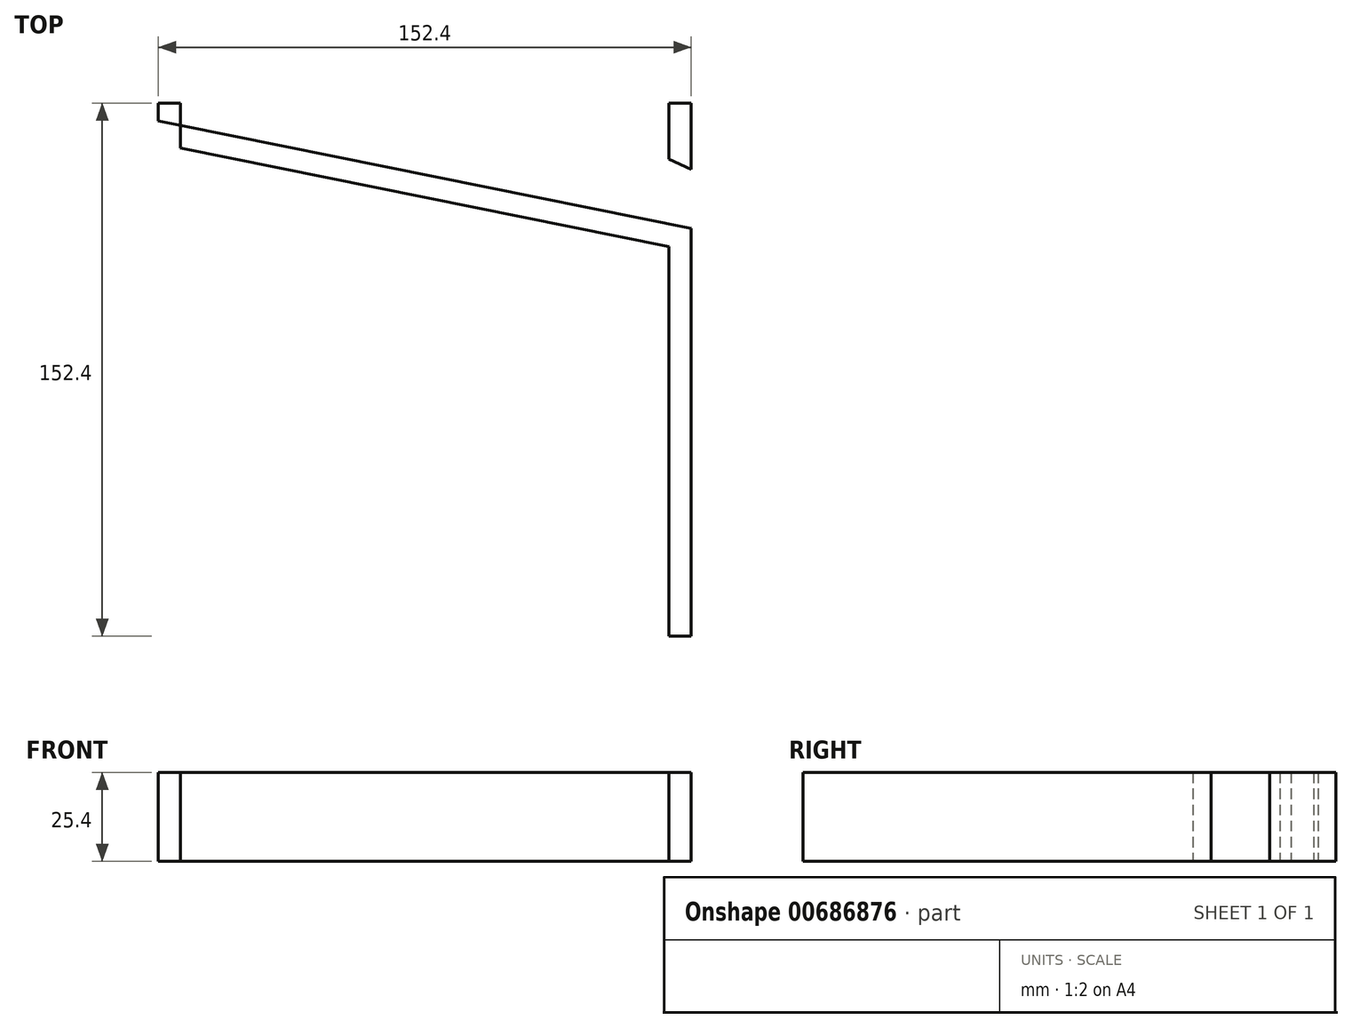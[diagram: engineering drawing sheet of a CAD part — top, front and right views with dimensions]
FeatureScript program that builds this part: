
annotation { "Feature Type Name" : "Feature", "Feature Type Description" : "" }
export const myFeature = defineFeature(function(context is Context, id is Id, definition is map)
    precondition{}
    {
        {
            var Q0;
            Q0=qCreatedBy(makeId("Top.planeOp"),FACE);
            var sketch = newSketch(context, id + "F0", { "sketchPlane" : qUnion([Q0])});
            skLineSegment(sketch, "E0.bottom", {"start": v(-76.85, 75.62) * mm, "end": v(-70.5, 75.62) * mm});
            skLineSegment(sketch, "E0.top", {"start": v(-30.3, -133.93) * mm, "end": v(-23.95, -133.93) * mm});
            skLineSegment(sketch, "E0.left", {"start": v(-76.85, 75.62) * mm, "end": v(-76.85, -76.78) * mm});
            skLineSegment(sketch, "E0.right", {"start": v(-70.5, 75.62) * mm, "end": v(-70.5, -76.78) * mm});
            skLineSegment(sketch, "E1.bottom", {"start": v(69.2, 75.62) * mm, "end": v(75.55, 75.62) * mm});
            skLineSegment(sketch, "E1.left", {"start": v(69.2, 75.62) * mm, "end": v(69.2, -76.78) * mm});
            skLineSegment(sketch, "E1.right", {"start": v(75.55, 75.62) * mm, "end": v(75.55, -76.78) * mm});
            skLineSegment(sketch, "E2.bottom", {"start": v(-70.5, 75.62) * mm, "end": v(69.2, 75.62) * mm});
            skLineSegment(sketch, "E2.top", {"start": v(-70.5, 69.27) * mm, "end": v(69.2, 69.27) * mm});
            skLineSegment(sketch, "E2.left", {"start": v(-70.5, 75.62) * mm, "end": v(-70.5, 69.27) * mm});
            skLineSegment(sketch, "E2.right", {"start": v(69.2, 75.62) * mm, "end": v(69.2, 69.27) * mm});
            skLineSegment(sketch, "E3.bottom", {"start": v(-76.85, 70.55) * mm, "end": v(75.55, 39.85) * mm});
            skLineSegment(sketch, "E3.top", {"start": v(-75.34, 63.76) * mm, "end": v(88.82, 30.7) * mm});
            skLineSegment(sketch, "E3.left", {"start": v(-70.5, 55.09) * mm, "end": v(-70.5, 48.74) * mm});
            skLineSegment(sketch, "E3.right", {"start": v(69.2, 55.09) * mm, "end": v(69.2, 48.74) * mm});
            skLineSegment(sketch, "E4", {"start": v(-76.85, -76.78) * mm, "end": v(-70.5, -76.78) * mm});
            skLineSegment(sketch, "E5", {"start": v(69.2, -76.78) * mm, "end": v(75.55, -76.78) * mm});
            skLineSegment(sketch, "E6", {"start": v(75.55, 22.85) * mm, "end": v(75.55, 16.2) * mm});
            skLineSegment(sketch, "E7.bottom", {"start": v(24, 80.14) * mm, "end": v(176.4, 10.74) * mm});
            skLineSegment(sketch, "E7.top", {"start": v(23.93, 73.2) * mm, "end": v(176.33, 3.8) * mm});
            skSolve(sketch);
        }
        {
            var Q0;
            {var subQ4=sQuery(id+"F0.wireOp",EDGE,"E2.left");Q0=makeQuery(id+"F0.imprint","IMPRINT",FACE,{"disambiguationData":[TD([[makeQuery(id+"F0.imprint","IMPRINT",EDGE,{"derivedFrom":subQ4}),1.0]])]});}
            var Q1;
            {var subQ2=sQuery(id+"F0.wireOp",EDGE,"E3.left");Q1=makeQuery(id+"F0.imprint","IMPRINT",FACE,{"disambiguationData":[TD([[makeQuery(id+"F0.imprint","IMPRINT",EDGE,{"derivedFrom":subQ2}),-1.0]])]});}
            var Q2;
            {var subQ0=sQuery(id+"F0.wireOp",EDGE,"E0.bottom");Q2=makeQuery(id+"F0.imprint","IMPRINT",FACE,{"disambiguationData":[TD([[makeQuery(id+"F0.imprint","IMPRINT",EDGE,{"derivedFrom":subQ0}),-1.0]])]});}
            var Q3;
            {var subQ3=sQuery(id+"F0.wireOp",EDGE,"E3.top");var subQ5=sQuery(id+"F0.wireOp",EDGE,"E1.left");var subQ6=makeQuery(id+"F0.imprint","INTERSECT",VERTEX,{"derivedFrom":[subQ5,subQ3]});Q3=makeQuery(id+"F0.imprint","IMPRINT",FACE,{"disambiguationData":[TD([[makeQuery(id+"F0.imprint","IMPRINT",EDGE,{"disambiguationData":[TD([[subQ6,1.0]])],"derivedFrom":subQ5}),-1.0]])]});}
            var Q4;
            {var subQ0=sQuery(id+"F0.wireOp",EDGE,"E2.right");Q4=makeQuery(id+"F0.imprint","IMPRINT",FACE,{"disambiguationData":[TD([[makeQuery(id+"F0.imprint","IMPRINT",EDGE,{"derivedFrom":subQ0}),-1.0]])]});}
            var Q5;
            {var subQ2=sQuery(id+"F0.wireOp",EDGE,"E1.bottom");Q5=makeQuery(id+"F0.imprint","IMPRINT",FACE,{"disambiguationData":[TD([[makeQuery(id+"F0.imprint","IMPRINT",EDGE,{"derivedFrom":subQ2}),-1.0]])]});}
            var Q6;
            {var subQ0=sQuery(id+"F0.wireOp",EDGE,"E3.right");var subQ1=sQuery(id+"F0.wireOp",EDGE,"E1.left");var subQ2=makeQuery(id+"F0.imprint","INTERSECT",VERTEX,{"disambiguationData":[OD(0.0)],"derivedFrom":[subQ1,subQ0]});Q6=makeQuery(id+"F0.imprint","IMPRINT",FACE,{"disambiguationData":[TD([[makeQuery(id+"F0.imprint","IMPRINT",EDGE,{"disambiguationData":[TD([[subQ2,1.0]])],"derivedFrom":subQ1}),1.0]])]});}
            var Q7;
            {var subQ0=sQuery(id+"F0.wireOp",EDGE,"E3.right");var subQ1=sQuery(id+"F0.wireOp",EDGE,"E1.left");var subQ2=makeQuery(id+"F0.imprint","INTERSECT",VERTEX,{"disambiguationData":[OD(1.0)],"derivedFrom":[subQ1,subQ0]});Q7=makeQuery(id+"F0.imprint","IMPRINT",FACE,{"disambiguationData":[TD([[makeQuery(id+"F0.imprint","IMPRINT",EDGE,{"disambiguationData":[TD([[subQ2,-1.0]])],"derivedFrom":subQ1}),1.0]])]});}
            var Q8;
            {var subQ0=sQuery(id+"F0.wireOp",EDGE,"E3.top");var subQ1=sQuery(id+"F0.wireOp",EDGE,"E1.left");var subQ2=makeQuery(id+"F0.imprint","INTERSECT",VERTEX,{"derivedFrom":[subQ1,subQ0]});Q8=makeQuery(id+"F0.imprint","IMPRINT",FACE,{"disambiguationData":[TD([[makeQuery(id+"F0.imprint","IMPRINT",EDGE,{"disambiguationData":[TD([[subQ2,1.0]])],"derivedFrom":subQ1}),1.0]])]});}
            var Q9;
            {var subQ5=sQuery(id+"F0.wireOp",EDGE,"E5");Q9=makeQuery(id+"F0.imprint","IMPRINT",FACE,{"disambiguationData":[TD([[makeQuery(id+"F0.imprint","IMPRINT",EDGE,{"derivedFrom":subQ5}),1.0]])]});}
            extrude(context, id + "F1", {"entities" : qUnion([Q0, Q1, Q2, Q3, Q4, Q5, Q6, Q7, Q8, Q9]), "depth" : 25.4 * mm, "offsetDistance" : 25.4 * mm});
        }
    });
